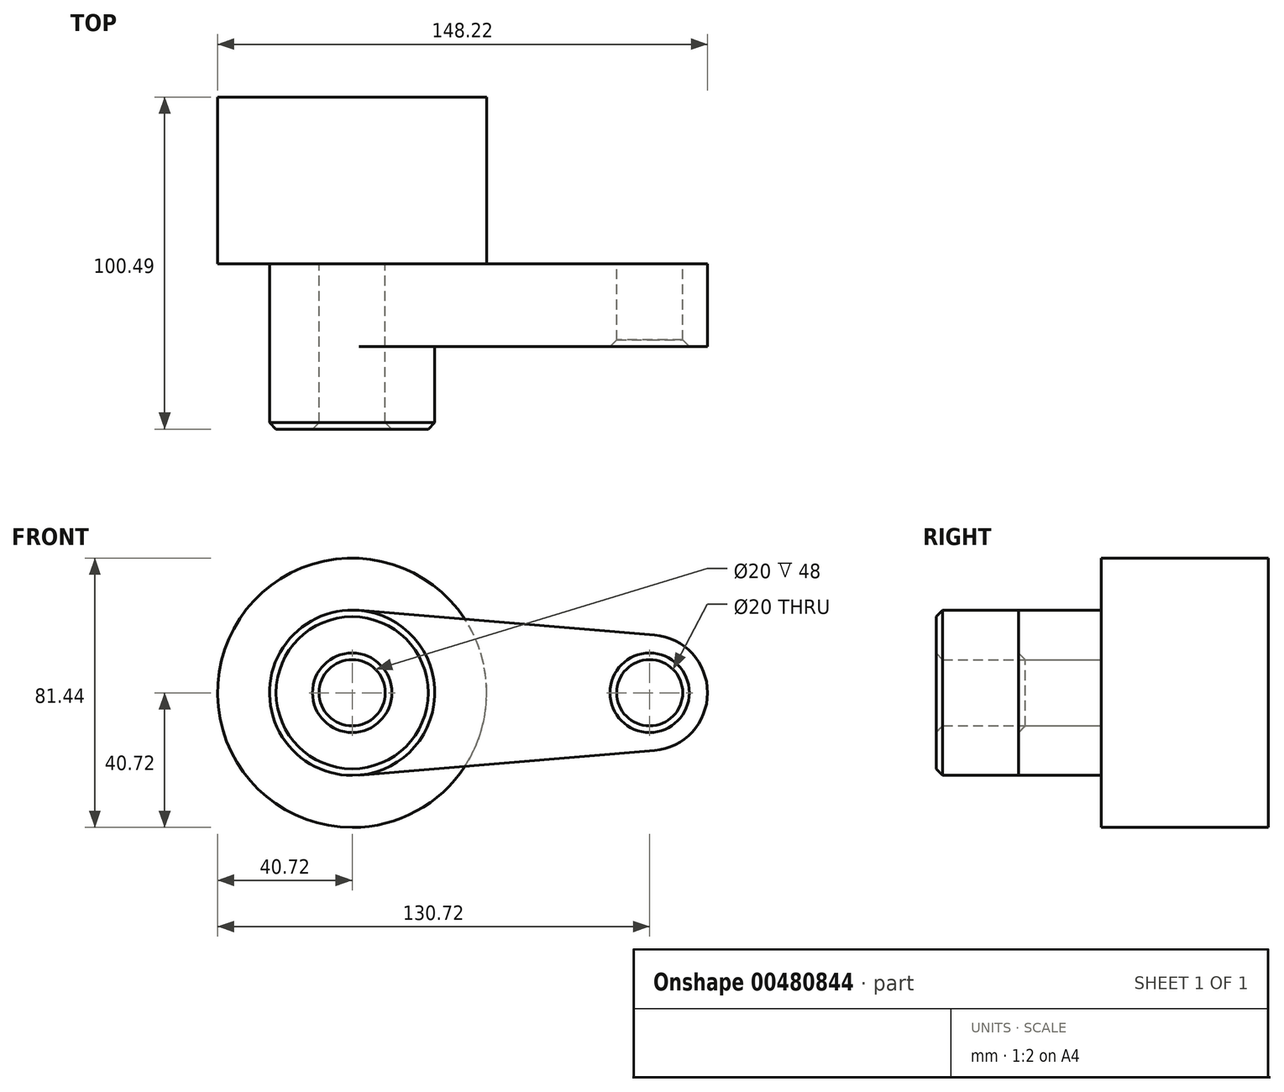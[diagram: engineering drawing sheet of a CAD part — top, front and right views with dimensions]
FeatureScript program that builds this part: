
annotation { "Feature Type Name" : "Feature", "Feature Type Description" : "" }
export const myFeature = defineFeature(function(context is Context, id is Id, definition is map)
    precondition{}
    {
        {
            var Q0;
            Q0=qCreatedBy(makeId("Front.planeOp"),FACE);
            var sketch = newSketch(context, id + "F0", { "sketchPlane" : qUnion([Q0])});
            skCircle(sketch, "E0", {"center": v(0, 0) * mm, "radius": 25 * mm});
            skCircle(sketch, "E1", {"center": v(90, 0) * mm, "radius": 17.5 * mm});
            skLineSegment(sketch, "E2", {"start": v(2.08, 24.91) * mm, "end": v(91.46, 17.44) * mm});
            skLineSegment(sketch, "E3", {"start": v(2.08, -24.91) * mm, "end": v(91.46, -17.44) * mm});
            skCircle(sketch, "E4", {"center": v(0, 0) * mm, "radius": 10 * mm});
            skCircle(sketch, "E5", {"center": v(90, 0) * mm, "radius": 10 * mm});
            skSolve(sketch);
        }
        {
            var Q0;
            Q0=qSketchRegion(id+"F0",true);
            extrude(context, id + "F1", {"entities" : qUnion([Q0]), "depth" : 25 * mm});
        }
        {
            var Q0;
            Q0=makeQuery(id+"F0.imprint","IMPRINT",FACE,{"disambiguationData":[TD([[makeQuery(id+"F0.imprint","IMPRINT",EDGE,{"derivedFrom":sQuery(id+"F0.wireOp",EDGE,"E4")}),-1.0]])]});
            extrude(context, id + "F2", {"entities" : qUnion([Q0]), "operationType" : NewBodyOperationType.ADD, "depth" : 50 * mm});
        }
        {
            var Q0;
            Q0=makeQuery(id+"F2.opExtrude","CAP_EDGE",EDGE,{"disambiguationData":[OSD([sQuery(id+"F0.wireOp",EDGE,"E0")])],"isStart":false});
            var Q1;
            Q1=makeQuery(id+"F2.opExtrude","CAP_EDGE",EDGE,{"disambiguationData":[OSD([sQuery(id+"F0.wireOp",EDGE,"E4")])],"isStart":false});
            var Q2;
            Q2=makeQuery(id+"F1.opExtrude","CAP_EDGE",EDGE,{"disambiguationData":[OSD([sQuery(id+"F0.wireOp",EDGE,"E5")])],"isStart":false});
            chamfer(context, id + "F3", {"entities" : qUnion([Q0, Q1, Q2]), "width" : 2 * mm, "tangentPropagation" : true});
        }
        {
            var Q0;
            Q0=qCreatedBy(makeId("Front.planeOp"),FACE);
            var sketch = newSketch(context, id + "F4", { "sketchPlane" : qUnion([Q0])});
            skCircle(sketch, "E6", {"center": v(0, 0) * mm, "radius": 40.72 * mm});
            skSolve(sketch);
        }
        {
            var Q0;
            Q0=makeQuery(id+"F4.imprint","IMPRINT",FACE,{"disambiguationData":[TD([[makeQuery(id+"F4.imprint","IMPRINT",EDGE,{"derivedFrom":sQuery(id+"F4.wireOp",EDGE,"E6")}),1.0]])]});
            var Q1;
            Q1=sQuery(id+"F4.wireOp",EDGE,"E6");
            extrude(context, id + "F5", {"entities" : qUnion([Q0]), "operationType" : NewBodyOperationType.ADD, "surfaceEntities" : qUnion([Q1]), "oppositeDirection" : true, "depth" : 50.5 * mm});
        }
    });
